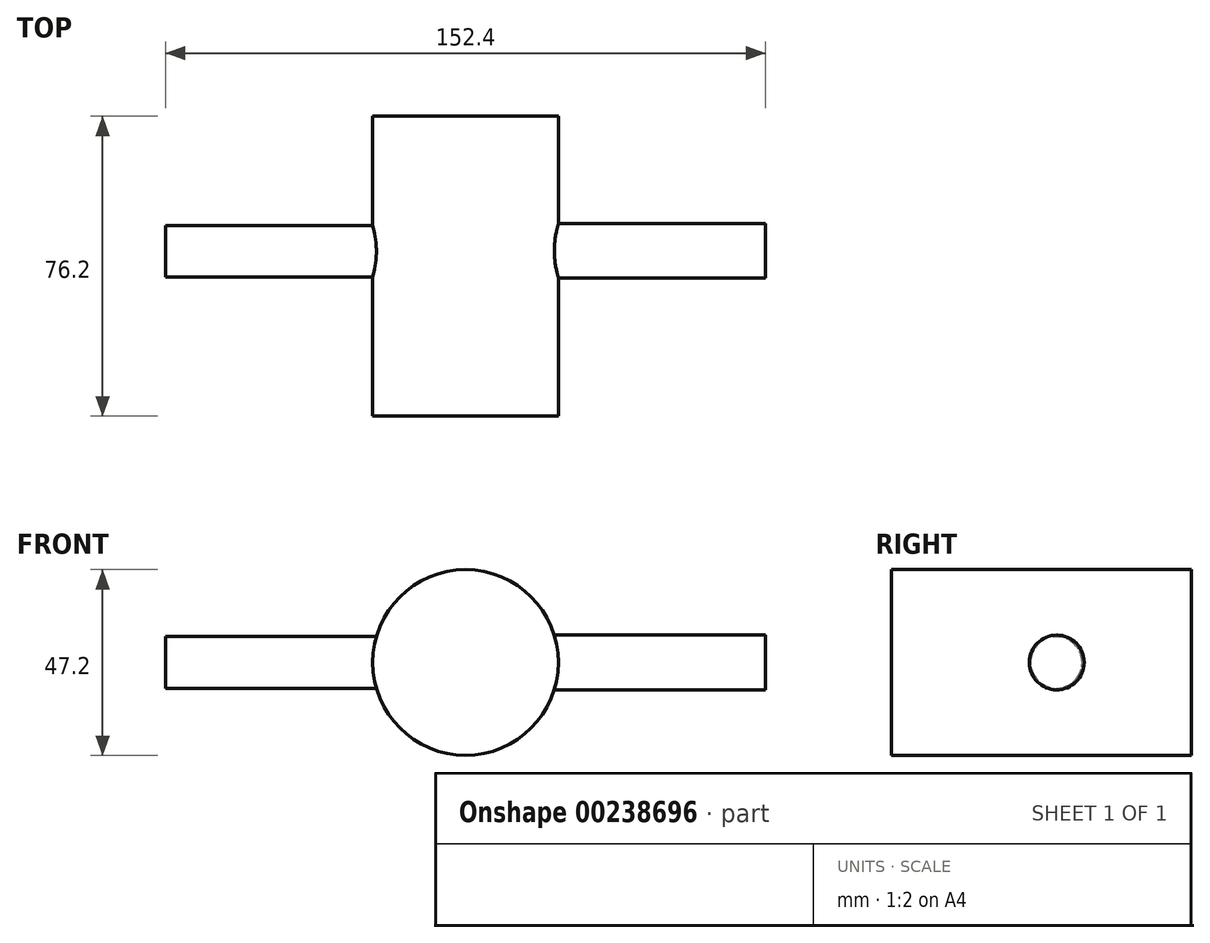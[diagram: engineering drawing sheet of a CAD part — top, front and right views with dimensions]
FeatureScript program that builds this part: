
annotation { "Feature Type Name" : "Feature", "Feature Type Description" : "" }
export const myFeature = defineFeature(function(context is Context, id is Id, definition is map)
    precondition{}
    {
        {
            var Q0;
            Q0=qCreatedBy(makeId("Front.planeOp"),FACE);
            var sketch = newSketch(context, id + "F0", { "sketchPlane" : qUnion([Q0])});
            skCircle(sketch, "E0", {"center": v(0, 0) * mm, "radius": 23.6 * mm});
            skSolve(sketch);
        }
        {
            var Q0;
            Q0 = qSketchRegion(id + "F0", true);
            extrude(context, id + "F1", {"entities" : qUnion([Q0]), "depth" : 76.2 * mm});
        }
        {
            var Q0;
            Q0=qCreatedBy(makeId("Right.planeOp"),FACE);
            var sketch = newSketch(context, id + "F2", { "sketchPlane" : qUnion([Q0])});
            skCircle(sketch, "E1", {"center": v(-34.2, 0) * mm, "radius": 6.96 * mm});
            skSolve(sketch);
        }
        {
            var Q0;
            Q0 = qSketchRegion(id + "F2", true);
            extrude(context, id + "F3", {"entities" : qUnion([Q0]), "operationType" : NewBodyOperationType.ADD, "depth" : 76.2 * mm});
        }
        {
            var Q0;
            Q0=qCreatedBy(makeId("Right.planeOp"),FACE);
            var sketch = newSketch(context, id + "F4", { "sketchPlane" : qUnion([Q0])});
            skCircle(sketch, "E2", {"center": v(-34.33, 0) * mm, "radius": 6.6 * mm});
            skSolve(sketch);
        }
        {
            var Q0;
            Q0 = qSketchRegion(id + "F4", true);
            extrude(context, id + "F5", {"entities" : qUnion([Q0]), "operationType" : NewBodyOperationType.ADD, "oppositeDirection" : true, "depth" : 76.2 * mm});
        }
    });
